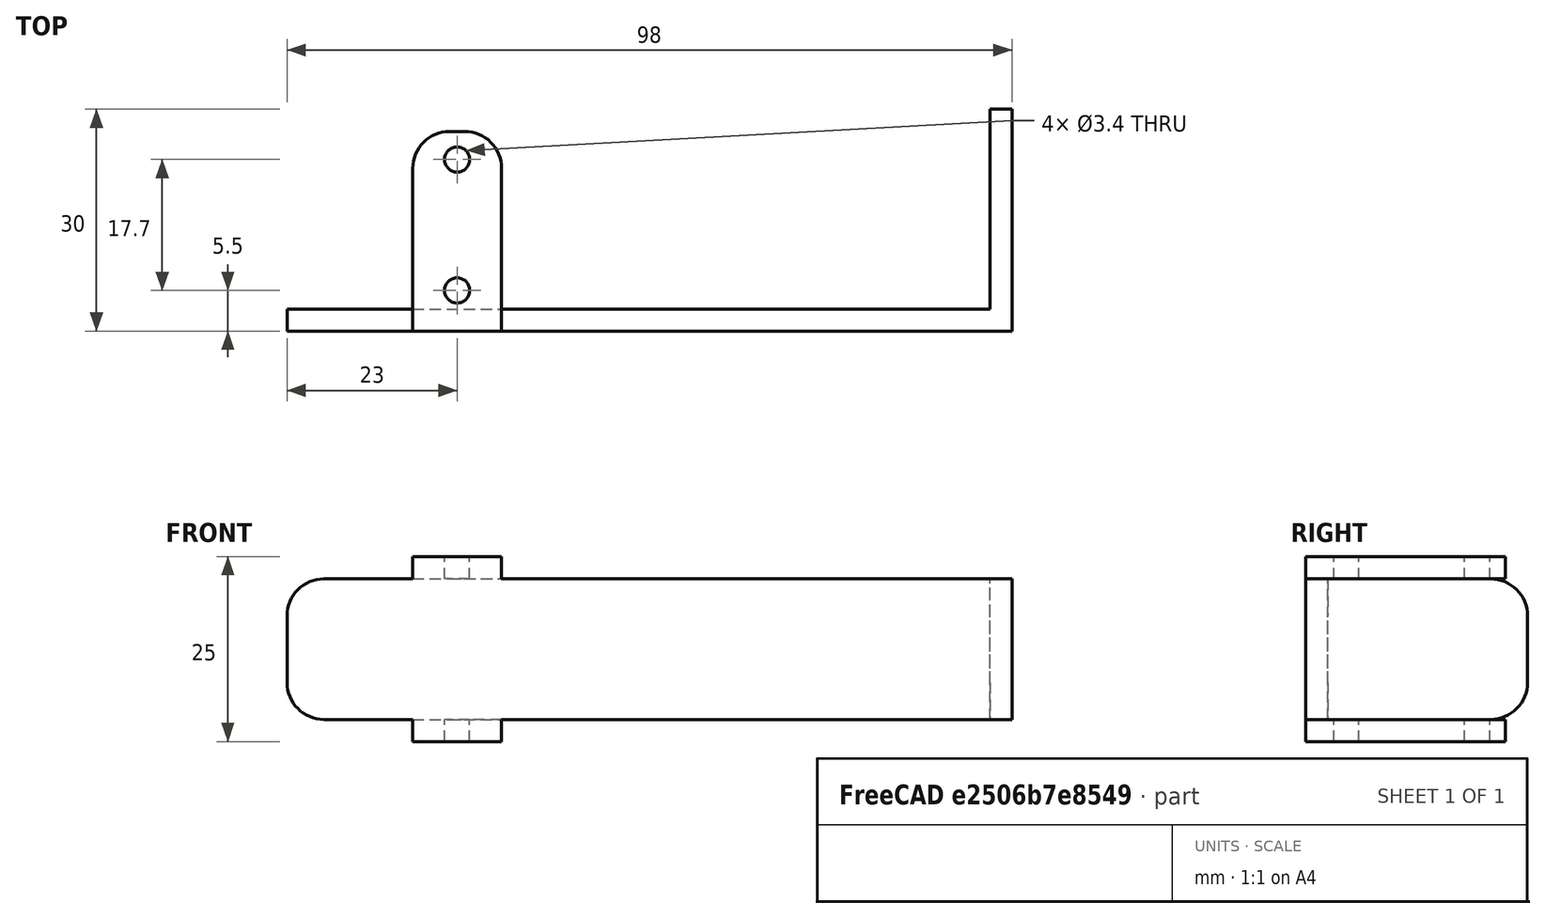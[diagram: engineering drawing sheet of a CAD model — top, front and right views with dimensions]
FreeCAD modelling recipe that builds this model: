
FCSTD DOCUMENT  (FreeCAD 0.15R4671 (Git))
Label: runner base
License: CreativeCommons Attribution-ShareAlike
LicenseURL: http://creativecommons.org/licenses/by-sa/4.0/
objects: Part::Box×4, Part::MultiFuse×2, Part::Cylinder×2, Part::Fillet×1, Part::Cut×1
note: 10 computed .brp shape members not serialized (recipe doc carries the construction recipe); baked Part::Feature solids carry a one-line shape summary decoded from their .brp

FEATURE [Part::Box] Box  label="Cube"
  Height = 19
  Length = 95
  Placement = pos=(-17,0,0) rot=(0,0,1;0rad)
  Width = 3
FEATURE [Part::Box] Box001  label="Cube001"
  Height = 3
  Length = 12
  Placement = pos=(0,0,-3) rot=(0,0,1;0rad)
  Width = 27
FEATURE [Part::Box] Box002  label="Cube002"
  Height = 3
  Length = 12
  Placement = pos=(0,0,19) rot=(0,0,1;0rad)
  Width = 27
FEATURE [Part::Box] Box003  label="Cube003"
  Height = 19
  Length = 3
  Placement = pos=(78,0,0) rot=(0,0,1;0rad)
  Width = 30
FEATURE [Part::MultiFuse] Fusion
  Shapes = -> [Box,Box003,Box001,Box002]
FEATURE [Part::Fillet] Fillet
  Base = -> Fusion
  Edges = 8 edges r=5: [Edge5,Edge6,Edge14,Edge17,Edge23,Edge32,Edge42,Edge48]
FEATURE [Part::Cylinder] Cylinder
  Angle = 360
  Height = 31
  Placement = pos=(6,5.5,-6) rot=(0,0,1;0rad)
  Radius = 1.7
FEATURE [Part::Cylinder] Cylinder001
  Angle = 360
  Height = 31
  Placement = pos=(6,23.2,-6) rot=(0,0,1;0rad)
  Radius = 1.7
FEATURE [Part::MultiFuse] Fusion001  label="orificios"
  Shapes = -> [Cylinder,Cylinder001]
FEATURE [Part::Cut] Cut
  Base = -> Fillet
  Tool = -> Fusion001
